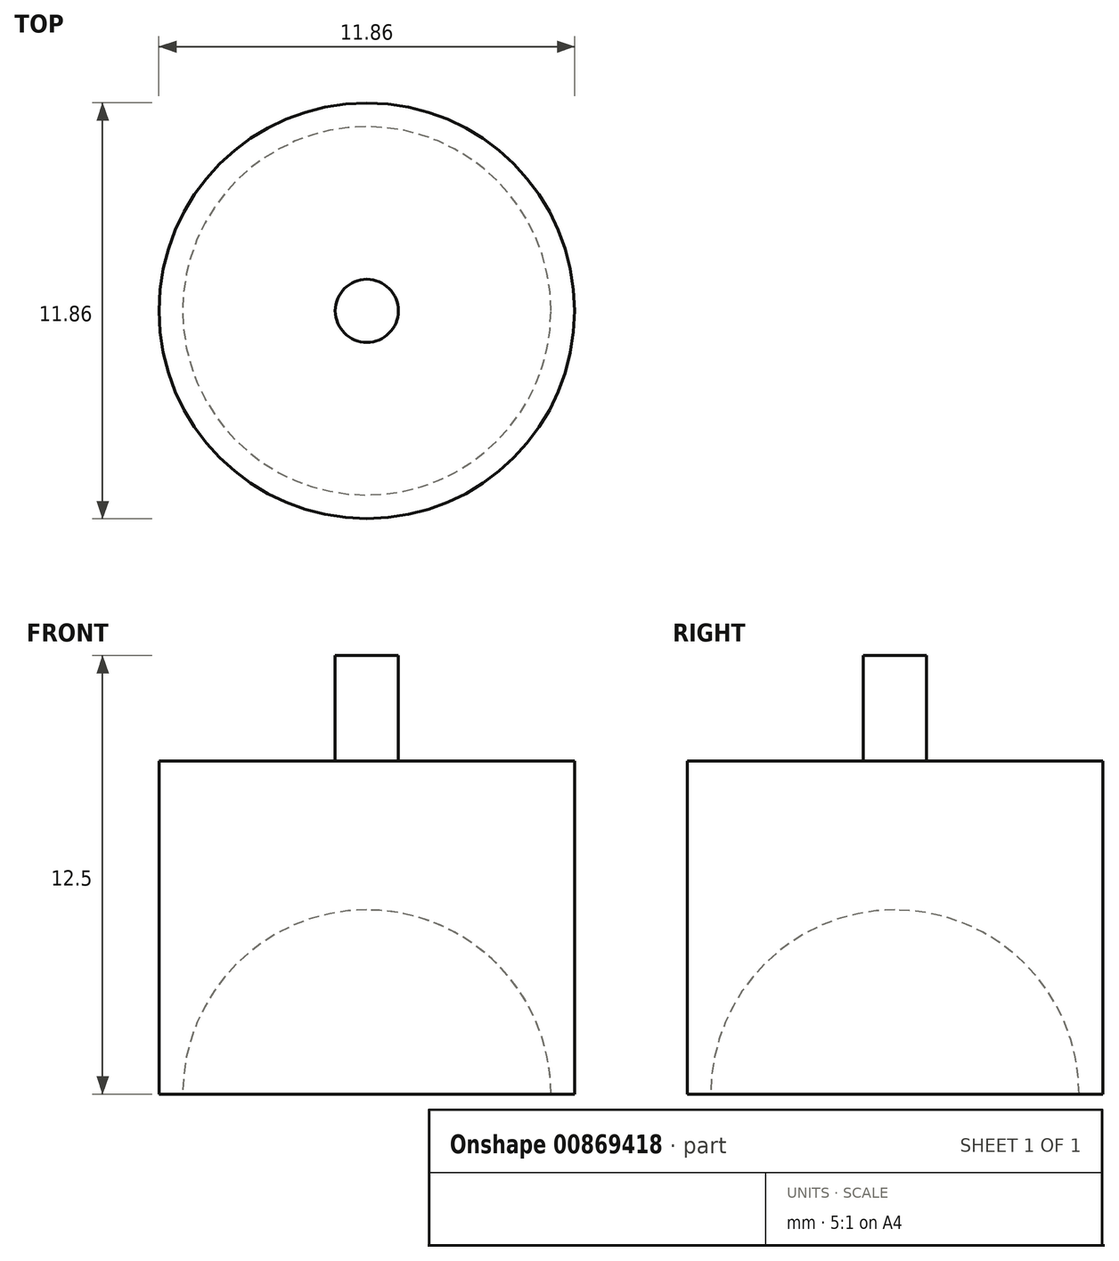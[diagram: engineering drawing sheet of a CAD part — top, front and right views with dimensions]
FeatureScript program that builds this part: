
annotation { "Feature Type Name" : "Feature", "Feature Type Description" : "" }
export const myFeature = defineFeature(function(context is Context, id is Id, definition is map)
    precondition{}
    {
        {
            var Q0;
            Q0=qCreatedBy(makeId("Top.planeOp"),FACE);
            var sketch = newSketch(context, id + "F0", { "sketchPlane" : qUnion([Q0])});
            skCircle(sketch, "E0", {"center": v(0, 0) * mm, "radius": 5.92 * mm});
            skSolve(sketch);
        }
        {
            var Q0;
            Q0=makeQuery(id+"F0.imprint","IMPRINT",FACE,{"disambiguationData":[TD([[makeQuery(id+"F0.imprint","IMPRINT",EDGE,{"derivedFrom":sQuery(id+"F0.wireOp",EDGE,"E0")}),1.0]])]});
            extrude(context, id + "F1", {"entities" : qUnion([Q0]), "depth" : 9.5 * mm, "offsetDistance" : 25 * mm});
        }
        {
            var Q0;
            Q0=makeQuery(id+"F1.opExtrude","CAP_FACE",FACE,{"disambiguationData":[OSD([sQuery(id+"F0.wireOp",EDGE,"E0")])],"isStart":false});
            var sketch = newSketch(context, id + "F2", { "sketchPlane" : qUnion([Q0])});
            skCircle(sketch, "E1", {"center": v(0, 0) * mm, "radius": 0.9 * mm});
            skSolve(sketch);
        }
        {
            var Q0;
            Q0=makeQuery(id+"F2.imprint","IMPRINT",FACE,{"disambiguationData":[TD([[makeQuery(id+"F2.imprint","IMPRINT",EDGE,{"derivedFrom":sQuery(id+"F2.wireOp",EDGE,"E1")}),1.0]])]});
            extrude(context, id + "F3", {"entities" : qUnion([Q0]), "operationType" : NewBodyOperationType.ADD, "depth" : 3 * mm, "offsetDistance" : 25 * mm});
        }
        {
            var Q0;
            Q0=qCreatedBy(makeId("Front.planeOp"),FACE);
            var sketch = newSketch(context, id + "F4", { "sketchPlane" : qUnion([Q0])});
            skArc(sketch, "E2", {"start": v(5.25, 0) * mm, "mid": v(3.71, 3.71) * mm, "end": v(0, 5.25) * mm});
            skLineSegment(sketch, "E3", {"start": v(0, 0) * mm, "end": v(0, 5.25) * mm});
            skLineSegment(sketch, "E4.0", {"start": v(0, 0) * mm, "end": v(5.25, 0) * mm});
            skPoint(sketch, "E5.orphan", {"position": v(-5.92, 0) * mm});
            skPoint(sketch, "E6.orphan", {"position": v(5.92, 0) * mm});
            skLineSegment(sketch, "E7", {"start": v(0, 5.25) * mm, "end": v(0, 9.52) * mm, "construction": true});
            skSolve(sketch);
        }
        {
            var Q0;
            Q0 = qSketchRegion(id + "F4", true);
            var Q1;
            Q1=sQuery(id+"F4.wireOp",EDGE,"E7");
            revolve(context, id + "F5", {"operationType" : NewBodyOperationType.REMOVE, "surfaceOperationType" : NewSurfaceOperationType.NEW, "entities" : qUnion([Q0]), "axis" : qUnion([Q1]), "revolveType" : RevolveType.FULL, "oppositeDirection" : true});
        }
    });
